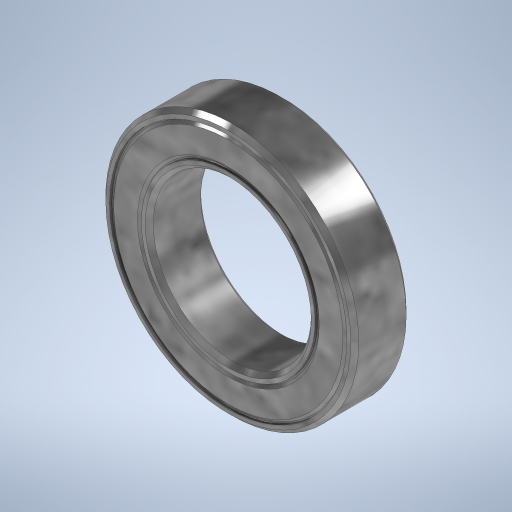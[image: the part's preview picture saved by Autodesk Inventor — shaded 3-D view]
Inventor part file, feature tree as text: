
AUTODESK INVENTOR PART (.ipt)
format: ipt  version: 2023 (Build 270158000, 158)  size: 391,168 bytes
history: native  units: mm
features: sketch x2, other x1, extrude x1, chamfer x1, revolve x1
ambient origin geometry x8: Origin, YZ Plane, XZ Plane, XY Plane, X Axis, Y Axis, Z Axis, Center Point
bodies: Body1 (feature_tree)
feature tree (6):
  other  "솔리드1"
  extrude  "돌출1"  Depth=20.0mm
  chamfer  "모따기1"  Distance=32.0mm
  revolve  "회전1"
  sketch  "스케치1"
  sketch  "스케치2"
